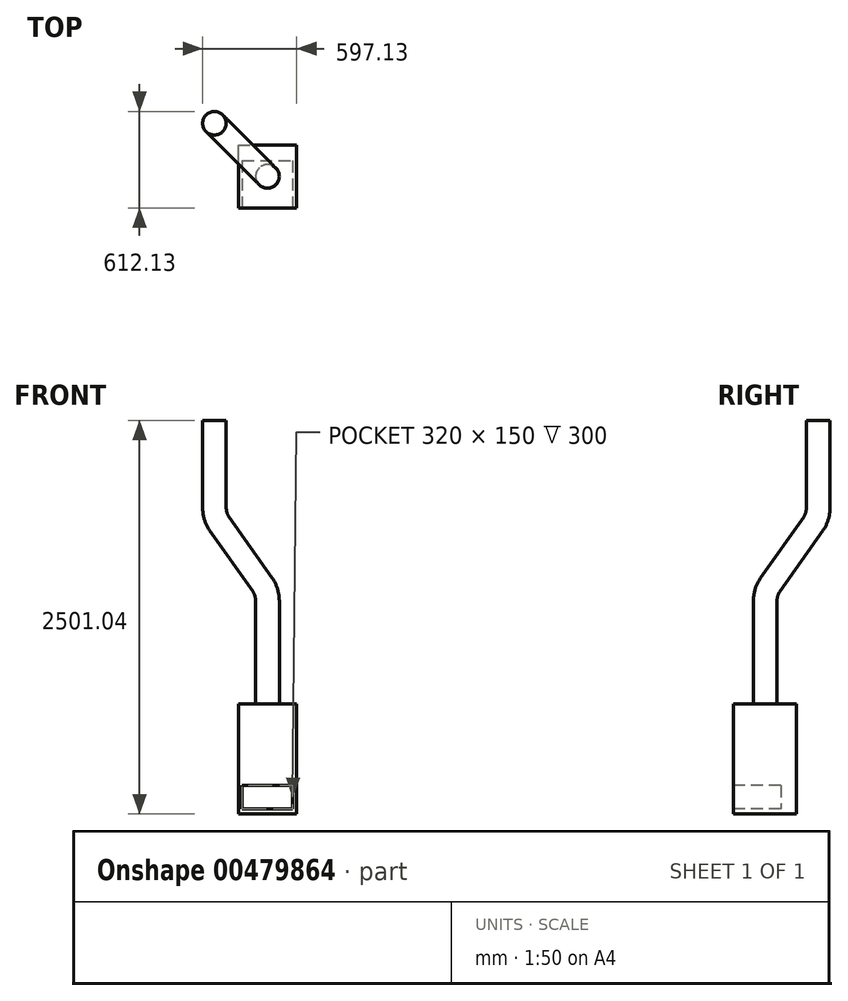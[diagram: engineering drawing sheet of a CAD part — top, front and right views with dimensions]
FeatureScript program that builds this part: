
annotation { "Feature Type Name" : "Feature", "Feature Type Description" : "" }
export const myFeature = defineFeature(function(context is Context, id is Id, definition is map)
    precondition{}
    {
        {
            var Q0;
            Q0=qCreatedBy(makeId("Front.planeOp"),FACE);
            var sketch = newSketch(context, id + "F0", { "sketchPlane" : qUnion([Q0])});
            skLineSegment(sketch, "E0.bottom", {"start": v(-185, 350) * mm, "end": v(185, 350) * mm});
            skLineSegment(sketch, "E0.top", {"start": v(-185, -350) * mm, "end": v(185, -350) * mm});
            skLineSegment(sketch, "E0.left", {"start": v(-185, 350) * mm, "end": v(-185, -350) * mm});
            skLineSegment(sketch, "E0.right", {"start": v(185, 350) * mm, "end": v(185, -350) * mm});
            skPoint(sketch, "E0.middle", {"position": v(0, 0) * mm});
            skSolve(sketch);
        }
        {
            var Q0;
            Q0=makeQuery(id+"F0.imprint","IMPRINT",FACE,{"disambiguationData":[TD([[makeQuery(id+"F0.imprint","IMPRINT",EDGE,{"derivedFrom":sQuery(id+"F0.wireOp",EDGE,"E0.bottom")}),-1.0]])]});
            extrude(context, id + "F1", {"entities" : qUnion([Q0]), "depth" : 400 * mm, "symmetric" : true});
        }
        {
            var Q0;
            Q0=qCreatedBy(makeId("Front.planeOp"),FACE);
            var sketch = newSketch(context, id + "F2", { "sketchPlane" : qUnion([Q0])});
            skLineSegment(sketch, "E1", {"start": v(0, 227.74) * mm, "end": v(0, -98.63) * mm});
            skSolve(sketch);
        }
        {
            var Q0;
            Q0=sQuery(id+"F2.wireOp",EDGE,"E1");
            var Q1;
            Q1=qCreatedBy(makeId("Front.planeOp"),FACE);
            cPlane(context, id + "F3", {"entities" : qUnion([Q0, Q1]), "cplaneType" : CPlaneType.LINE_ANGLE, "offset" : 25 * mm, "angle" : 225 * degree, "width" : 150 * mm, "height" : 150 * mm});
        }
        {
            var Q0;
            Q0=qCreatedBy(id+"F3.planeOp",FACE);
            var sketch = newSketch(context, id + "F4", { "sketchPlane" : qUnion([Q0])});
            skLineSegment(sketch, "E2", {"start": v(0, 350) * mm, "end": v(0, 1000) * mm});
            skLineSegment(sketch, "E3", {"start": v(-43.93, 1106.07) * mm, "end": v(-432.84, 1494.97) * mm});
            skLineSegment(sketch, "E4", {"start": v(-476.78, 1601.04) * mm, "end": v(-476.78, 2151.04) * mm});
            skPoint(sketch, "E5.visualSharp", {"position": v(-476.78, 1538.9) * mm});
            skArc(sketch, "E5.filletArc", {"start": v(-476.78, 1601.04) * mm, "mid": v(-465.36, 1543.64) * mm, "end": v(-432.84, 1494.97) * mm});
            skPoint(sketch, "E6.visualSharp", {"position": v(0, 1062.13) * mm});
            skArc(sketch, "E6.filletArc", {"start": v(0, 1000) * mm, "mid": v(-11.42, 1057.4) * mm, "end": v(-43.93, 1106.07) * mm});
            skSolve(sketch);
        }
        {
            var Q0;
            Q0=makeQuery(id+"F1.opExtrude","SWEPT_FACE",FACE,{"disambiguationData":[OSD([sQuery(id+"F0.wireOp",EDGE,"E0.bottom")])]});
            var sketch = newSketch(context, id + "F5", { "sketchPlane" : qUnion([Q0])});
            skCircle(sketch, "E7", {"center": v(0, 0) * mm, "radius": 75 * mm});
            skSolve(sketch);
        }
        {
            var Q0;
            Q0 = qSketchRegion(id + "F5", true);
            var Q1;
            Q1 = qBodyType(qCreatedBy(id + "F4" ,EDGE), BodyType.WIRE);
            sweep(context, id + "F6", {"operationType" : NewBodyOperationType.ADD, "profiles" : qUnion([Q0]), "path" : qUnion([Q1])});
        }
        {
            var Q0;
            Q0=makeQuery(id+"F1.opExtrude","CAP_FACE",FACE,{"disambiguationData":[OSD([sQuery(id+"F0.wireOp",EDGE,"E0.bottom"),sQuery(id+"F0.wireOp",EDGE,"E0.top"),sQuery(id+"F0.wireOp",EDGE,"E0.left"),sQuery(id+"F0.wireOp",EDGE,"E0.right")])],"isStart":false});
            var sketch = newSketch(context, id + "F7", { "sketchPlane" : qUnion([Q0])});
            skLineSegment(sketch, "E8.bottom", {"start": v(-160, -168.05) * mm, "end": v(160, -168.05) * mm});
            skLineSegment(sketch, "E8.top", {"start": v(-160, -318.05) * mm, "end": v(160, -318.05) * mm});
            skLineSegment(sketch, "E8.left", {"start": v(-160, -168.05) * mm, "end": v(-160, -318.05) * mm});
            skLineSegment(sketch, "E8.right", {"start": v(160, -168.05) * mm, "end": v(160, -318.05) * mm});
            skPoint(sketch, "E8.middle", {"position": v(0, -243.05) * mm});
            skSolve(sketch);
        }
        {
            var Q0;
            Q0 = qSketchRegion(id + "F7", true);
            extrude(context, id + "F8", {"entities" : qUnion([Q0]), "operationType" : NewBodyOperationType.REMOVE, "oppositeDirection" : true, "depth" : 300 * mm});
        }
    });
